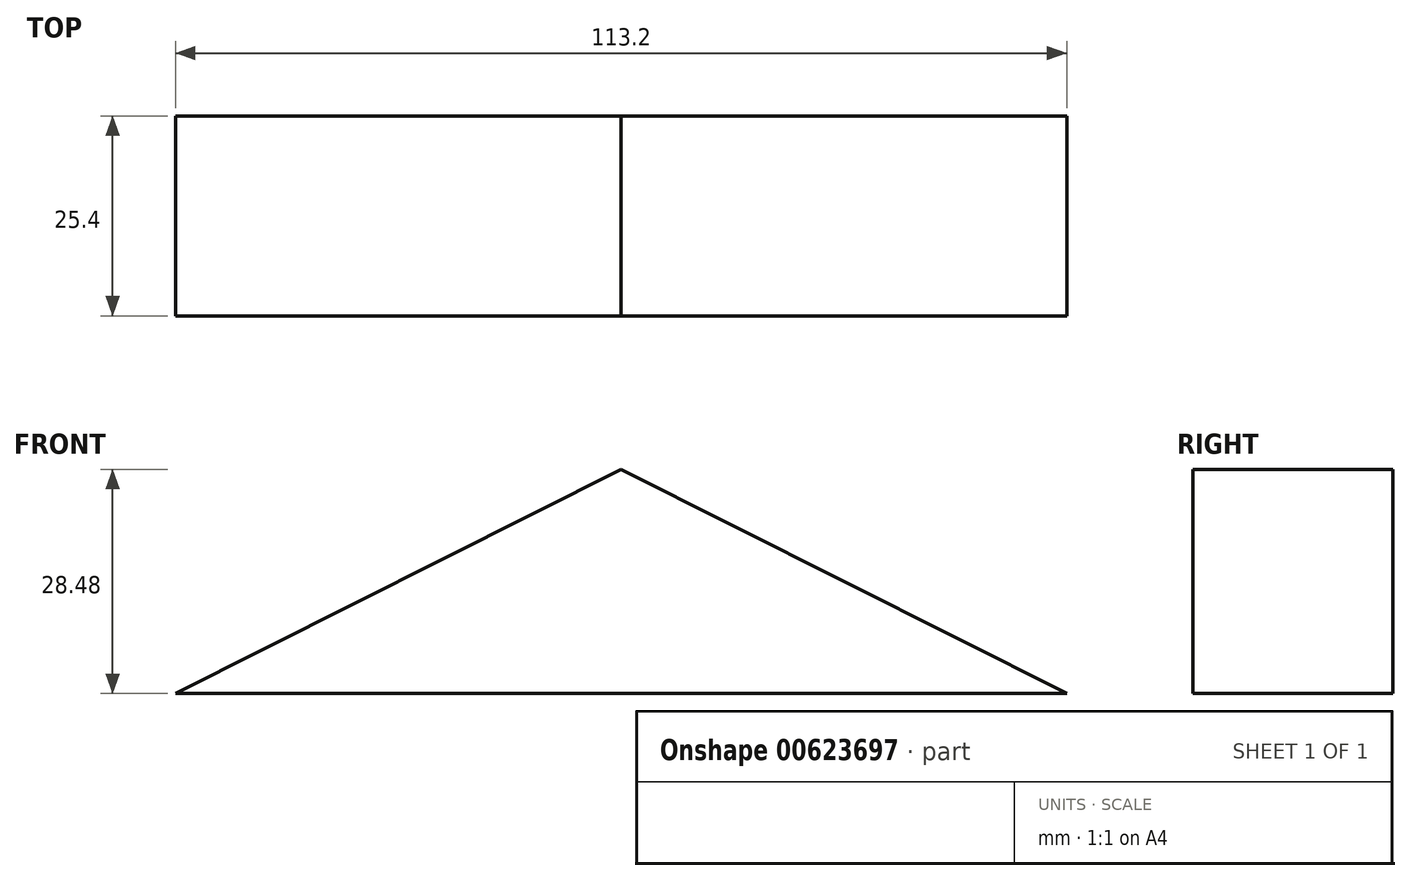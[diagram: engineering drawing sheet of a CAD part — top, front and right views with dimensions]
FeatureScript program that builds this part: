
annotation { "Feature Type Name" : "Feature", "Feature Type Description" : "" }
export const myFeature = defineFeature(function(context is Context, id is Id, definition is map)
    precondition{}
    {
        {
            var Q0;
            Q0=qCreatedBy(makeId("Front.planeOp"),FACE);
            var sketch = newSketch(context, id + "F0", { "sketchPlane" : qUnion([Q0])});
            skLineSegment(sketch, "E0", {"start": v(-56.72, 9.35) * mm, "end": v(56.48, 9.35) * mm});
            skLineSegment(sketch, "E1", {"start": v(-56.72, 9.35) * mm, "end": v(0, 37.9) * mm});
            skLineSegment(sketch, "E2", {"start": v(-0.12, 9.35) * mm, "end": v(-0.12, 63.86) * mm, "construction": true});
            skLineSegment(sketch, "E3.MirrorCS", {"start": v(56.48, 9.35) * mm, "end": v(-0.25, 37.9) * mm});
            skSolve(sketch);
        }
        {
            var Q0;
            Q0 = qSketchRegion(id + "F0", true);
            extrude(context, id + "F1", {"entities" : qUnion([Q0]), "depth" : 25.4 * mm, "offsetDistance" : 25.4 * mm});
        }
    });
